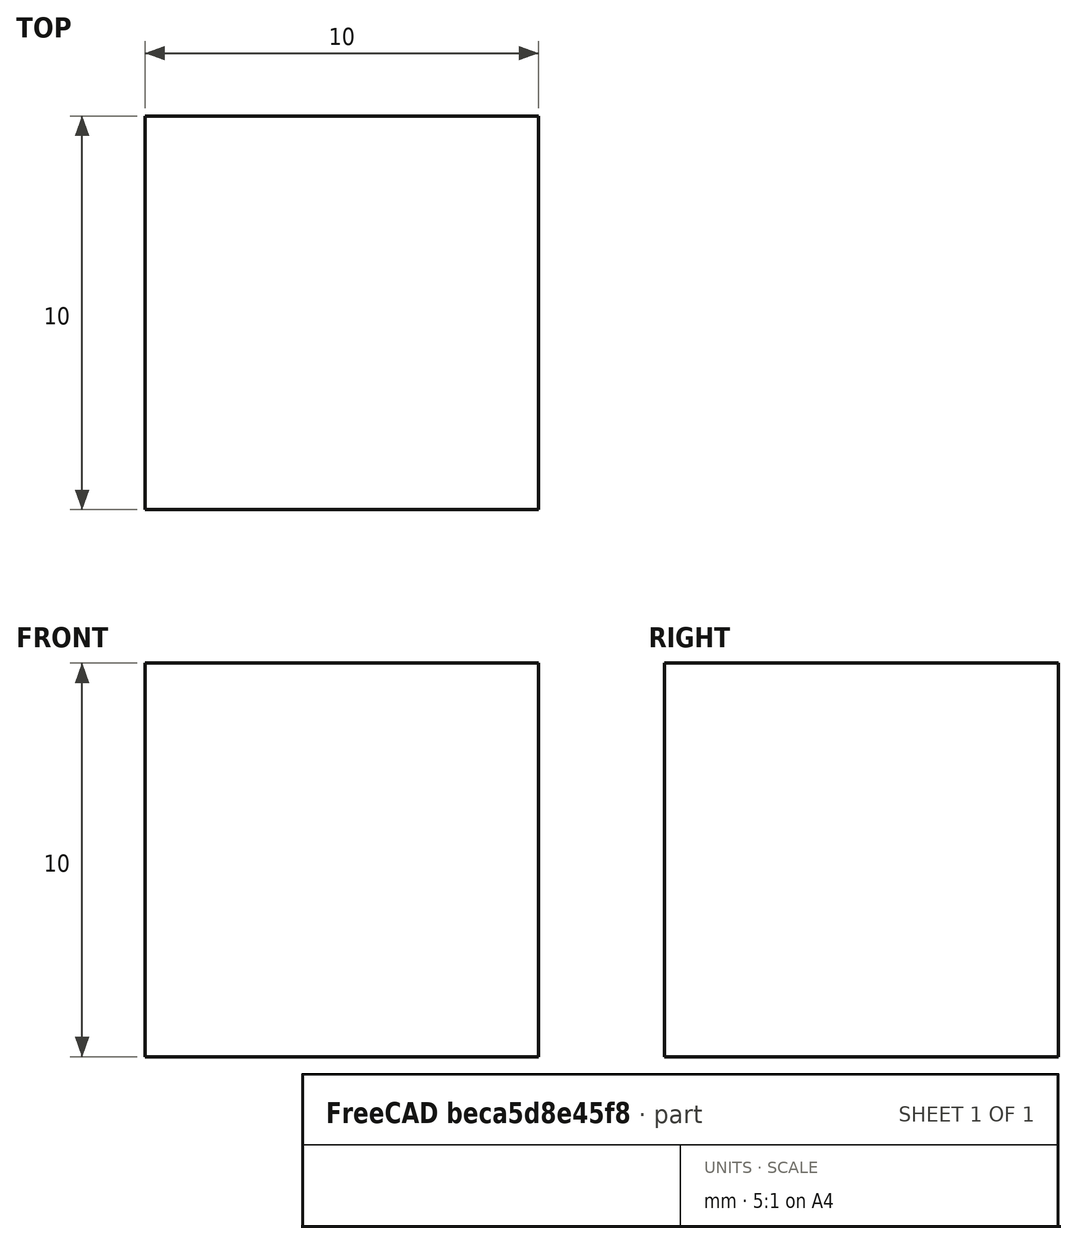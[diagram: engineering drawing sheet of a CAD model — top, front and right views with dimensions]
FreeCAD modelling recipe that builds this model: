
FCSTD DOCUMENT  (FreeCAD 0.21R33694 (Git))
Label: tensile_test
License: All rights reserved
LicenseURL: http://en.wikipedia.org/wiki/All_rights_reserved
objects: Part::Box×1, Fem::ConstraintFixed×1, App::MaterialObjectPython×1, Fem::FemSolverObjectPython×1, Fem::ConstraintPressure×1, Fem::FemMeshObjectPython×1, Fem::FemAnalysis×1
note: 1 computed .brp shape members not serialized (recipe doc carries the construction recipe); baked Part::Feature solids carry a one-line shape summary decoded from their .brp

FEATURE [Part::Box] Box  label="Cube"
  AttacherType = Attacher::AttachEngine3D
  Height = 10
  Length = 10
  Width = 10
FEATURE [Fem::ConstraintFixed] ConstraintFixed
  NormalDirection = (0,0,-1)
  Normals = (9) [(0,0,-1),(0,0,-1),(0,0,-1),(0,0,-1),(0,0,-1),(0,0,-1),(0,0,-1),(0,0,-1),(0,0,-1)]
  Points = (9) [(0,0,0),(5,0,0),(10,0,0),(0,5,0),(5,5,0),(10,5,0),(0,10,0),(5,10,0),(10,10,0)]
  References = -> [Box]
FEATURE [App::MaterialObjectPython] MaterialSolid  # material (typed FeaturePython)
  Category = 0
  Material = AuthorAndLicense=(c) 2014 M. Münch - GNU Lesser General Public License (LGPL); CardName=Steel-St-E-315; Density=7800 kg/m^3; Father=Metal; KindOfMaterial=Fine grain steel; KindOfMaterialDE=Feinkornstahl; MaterialNumber=1.0505; Name=St E 315; NameDE=St E 315; Norm=DIN 17102; PoissonRatio=0.3; ShearModulus=81000 MPa; ThermalExpansionCoefficient=0.000011 m/m/K; UltimateStrain=0; UltimateTensileStrength=440 MPa; YieldStrength=320 MPa; YoungsModulus=210000 MPa
FEATURE [Fem::FemSolverObjectPython] SolverCcxTools  # FEM object (typed FeaturePython)
  AnalysisType = 0
  BeamShellResultOutput3D = false
  BucklingFactors = 1
  EigenmodeHighLimit = 1000000
  EigenmodeLowLimit = 0
  EigenmodesCount = 10
  GeometricalNonlinearity = 0
  IterationsControlParameterCutb = 0.25,0.5,0.75,0.85,,,1.5,
  IterationsControlParameterIter = 4,8,9,200,10,400,,200,,
  IterationsControlParameterTimeUse = false
  IterationsThermoMechMaximum = 2000
  IterationsUserDefinedIncrementations = false
  IterationsUserDefinedTimeStepLength = false
  MaterialNonlinearity = 0
  MatrixSolverType = 0
  SplitInputWriter = false
  ThermoMechSteadyState = true
  TimeEnd = 1
  TimeInitialStep = 0.01
FEATURE [Fem::ConstraintPressure] ConstraintPressure
  NormalDirection = (0,0,1)
  Normals = (9) [(0,0,1),(0,0,1),(0,0,1),(0,0,1),(0,0,1),(0,0,1),(0,0,1),(0,0,1),(0,0,1)]
  Points = (9) [(0,0,10),(5,0,10),(10,0,10),(0,5,10),(5,5,10),(10,5,10),(0,10,10),(5,10,10),(10,10,10)]
  Pressure = 1
  References = -> [Box]
  Reversed = true
FEATURE [Fem::FemMeshObjectPython] FEMMeshGmsh  # FEM object (typed FeaturePython)
  Algorithm2D = 0
  Algorithm3D = 0
  CharacteristicLengthMax = 0
  CharacteristicLengthMin = 10
  CoherenceMesh = true
  ElementDimension = 0
  ElementOrder = 1
  GeometryTolerance = 1e-06
  GroupsOfNodes = false
  HighOrderOptimize = 0
  MeshSizeFromCurvature = 12
  OptimizeNetgen = false
  OptimizeStd = true
  Part = -> Box
  RecombinationAlgorithm = 0
  Recombine3DAll = false
  RecombineAll = false
  SecondOrderLinear = false
FEATURE [Fem::FemAnalysis] Analysis
  Group = -> [ConstraintFixed,MaterialSolid,SolverCcxTools,ConstraintPressure,FEMMeshGmsh]
